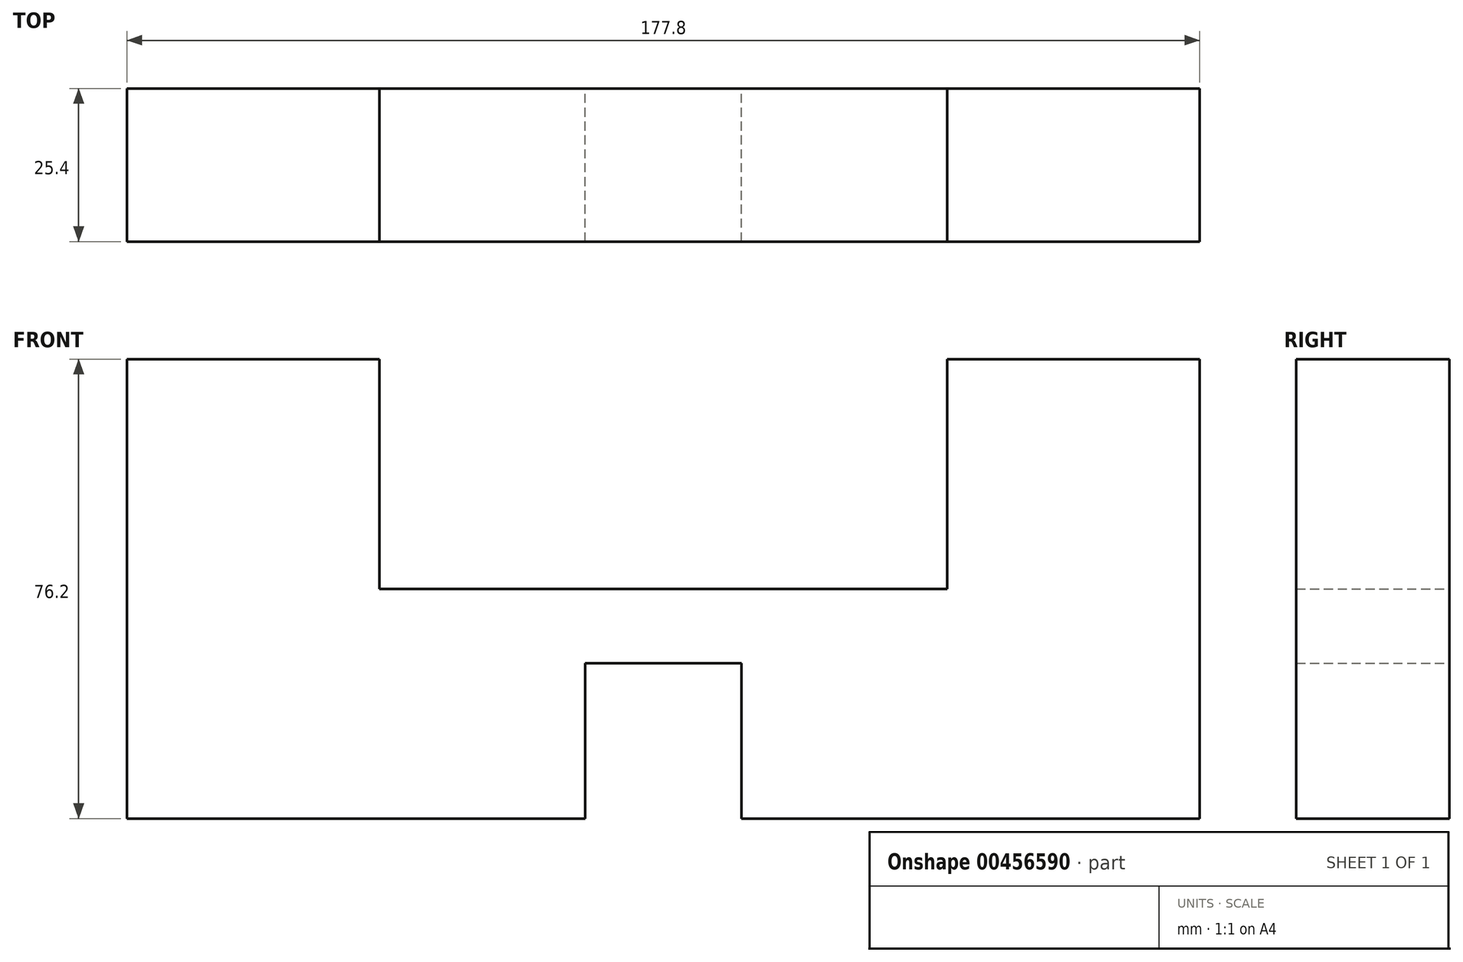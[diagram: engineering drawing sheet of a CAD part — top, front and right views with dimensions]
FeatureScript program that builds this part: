
annotation { "Feature Type Name" : "Feature", "Feature Type Description" : "" }
export const myFeature = defineFeature(function(context is Context, id is Id, definition is map)
    precondition{}
    {
        {
            var Q0;
            Q0=qCreatedBy(makeId("Front.planeOp"),FACE);
            var sketch = newSketch(context, id + "F0", { "sketchPlane" : qUnion([Q0])});
            skLineSegment(sketch, "E0.bottom", {"start": v(-88.9, 25.02) * mm, "end": v(-47.05, 25.02) * mm});
            skLineSegment(sketch, "E0.top", {"start": v(-88.9, -51.18) * mm, "end": v(-41.57, -51.18) * mm});
            skLineSegment(sketch, "E0.left", {"start": v(-88.9, 25.02) * mm, "end": v(-88.9, -51.18) * mm});
            skLineSegment(sketch, "E0.right", {"start": v(-47.05, 25.02) * mm, "end": v(-47.05, -13.08) * mm});
            skLineSegment(sketch, "E1.bottom", {"start": v(-47.05, -13.08) * mm, "end": v(0, -13.08) * mm});
            skLineSegment(sketch, "E1.top", {"start": v(-88.9, -51.18) * mm, "end": v(0, -51.18) * mm});
            skLineSegment(sketch, "E1.left", {"start": v(-88.9, -30.67) * mm, "end": v(-88.9, -51.18) * mm});
            skLineSegment(sketch, "E2.filletArc", {"start": v(-47.05, -13.08) * mm, "end": v(-47.05, -13.08) * mm});
            skLineSegment(sketch, "E3.MirrorCS", {"start": v(47.05, 25.02) * mm, "end": v(47.05, -13.08) * mm});
            skLineSegment(sketch, "E4.MirrorCS", {"start": v(88.9, 25.02) * mm, "end": v(47.05, 25.02) * mm});
            skLineSegment(sketch, "E5.MirrorCS", {"start": v(88.9, 25.02) * mm, "end": v(88.9, -51.18) * mm});
            skLineSegment(sketch, "E6.MirrorCS", {"start": v(47.05, -13.08) * mm, "end": v(0, -13.08) * mm});
            skLineSegment(sketch, "E7.MirrorCS", {"start": v(88.9, -51.18) * mm, "end": v(0, -51.18) * mm});
            skLineSegment(sketch, "E8.MirrorCS", {"start": v(47.05, -13.08) * mm, "end": v(47.05, -13.08) * mm});
            skSolve(sketch);
        }
        {
            var Q0;
            Q0=qSketchRegion(id+"F0",true);
            extrude(context, id + "F1", {"entities" : qUnion([Q0]), "depth" : 25.4 * mm});
        }
        {
            var Q0;
            Q0=qCreatedBy(makeId("Front.planeOp"),FACE);
            var sketch = newSketch(context, id + "F2", { "sketchPlane" : qUnion([Q0])});
            skLineSegment(sketch, "E9.bottom", {"start": v(-12.95, -25.4) * mm, "end": v(12.95, -25.4) * mm});
            skLineSegment(sketch, "E9.top", {"start": v(-12.95, -51.18) * mm, "end": v(12.95, -51.18) * mm});
            skLineSegment(sketch, "E9.left", {"start": v(-12.95, -25.4) * mm, "end": v(-12.95, -51.18) * mm});
            skLineSegment(sketch, "E9.right", {"start": v(12.95, -25.4) * mm, "end": v(12.95, -51.18) * mm});
            skSolve(sketch);
        }
        {
            var Q0;
            Q0=qSketchRegion(id+"F2",true);
            extrude(context, id + "F3", {"entities" : qUnion([Q0]), "operationType" : NewBodyOperationType.REMOVE, "depth" : 4 * mm});
        }
        {
            var Q0;
            Q0=qSketchRegion(id+"F2",true);
            extrude(context, id + "F4", {"entities" : qUnion([Q0]), "operationType" : NewBodyOperationType.REMOVE, "endBound" : BoundingType.THROUGH_ALL, "depth" : 25 * mm});
        }
    });
